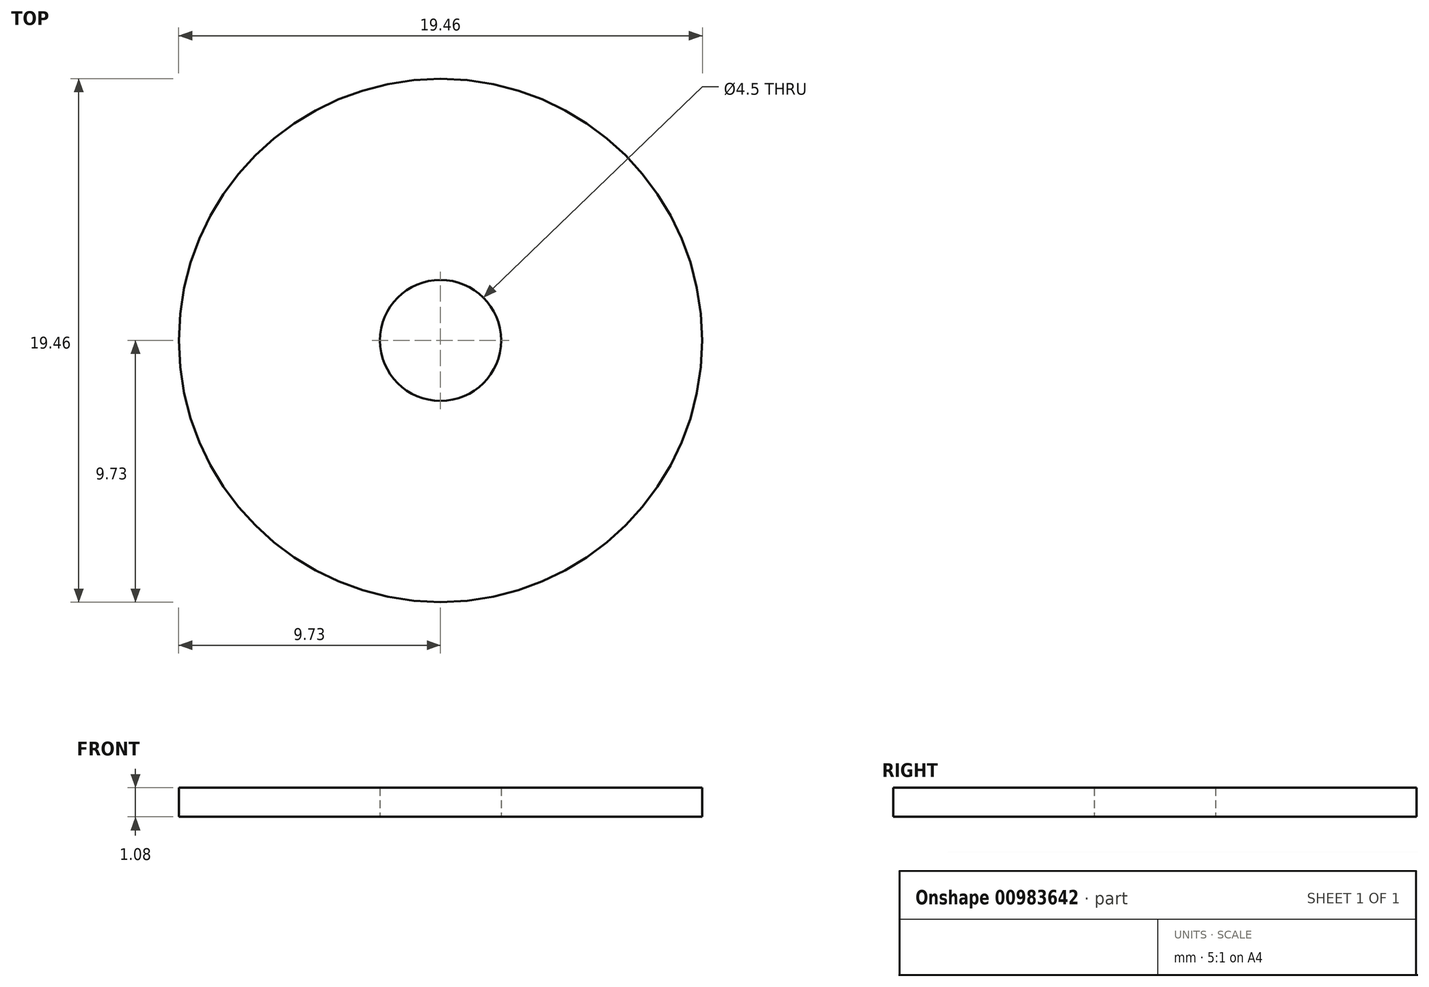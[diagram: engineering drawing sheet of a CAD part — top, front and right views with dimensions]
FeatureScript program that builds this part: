
annotation { "Feature Type Name" : "Feature", "Feature Type Description" : "" }
export const myFeature = defineFeature(function(context is Context, id is Id, definition is map)
    precondition{}
    {
        {
            assignVariable(context, id + "F0", {"name" : "RingH", "anyValue" : 1.08});
        }
        {
            var Q0;
            Q0=qCreatedBy(makeId("Top.planeOp"),FACE);
            var sketch = newSketch(context, id + "F1", { "sketchPlane" : qUnion([Q0])});
            skCircle(sketch, "E0", {"center": v(0, 0) * mm, "radius": 9.72 * mm});
            skCircle(sketch, "E1", {"center": v(0, 0) * mm, "radius": 2.25 * mm});
            skSolve(sketch);
        }
        {
            var Q0;
            Q0=makeQuery(id+"F1.imprint","IMPRINT",FACE,{"disambiguationData":[TD([[makeQuery(id+"F1.imprint","IMPRINT",EDGE,{"derivedFrom":sQuery(id+"F1.wireOp",EDGE,"E0")}),1.0]])]});
            extrude(context, id + "F2", {"entities" : qUnion([Q0]), "depth" : (getVariable(context, 'RingH')) * mm, "offsetDistance" : 25 * mm});
        }
    });
